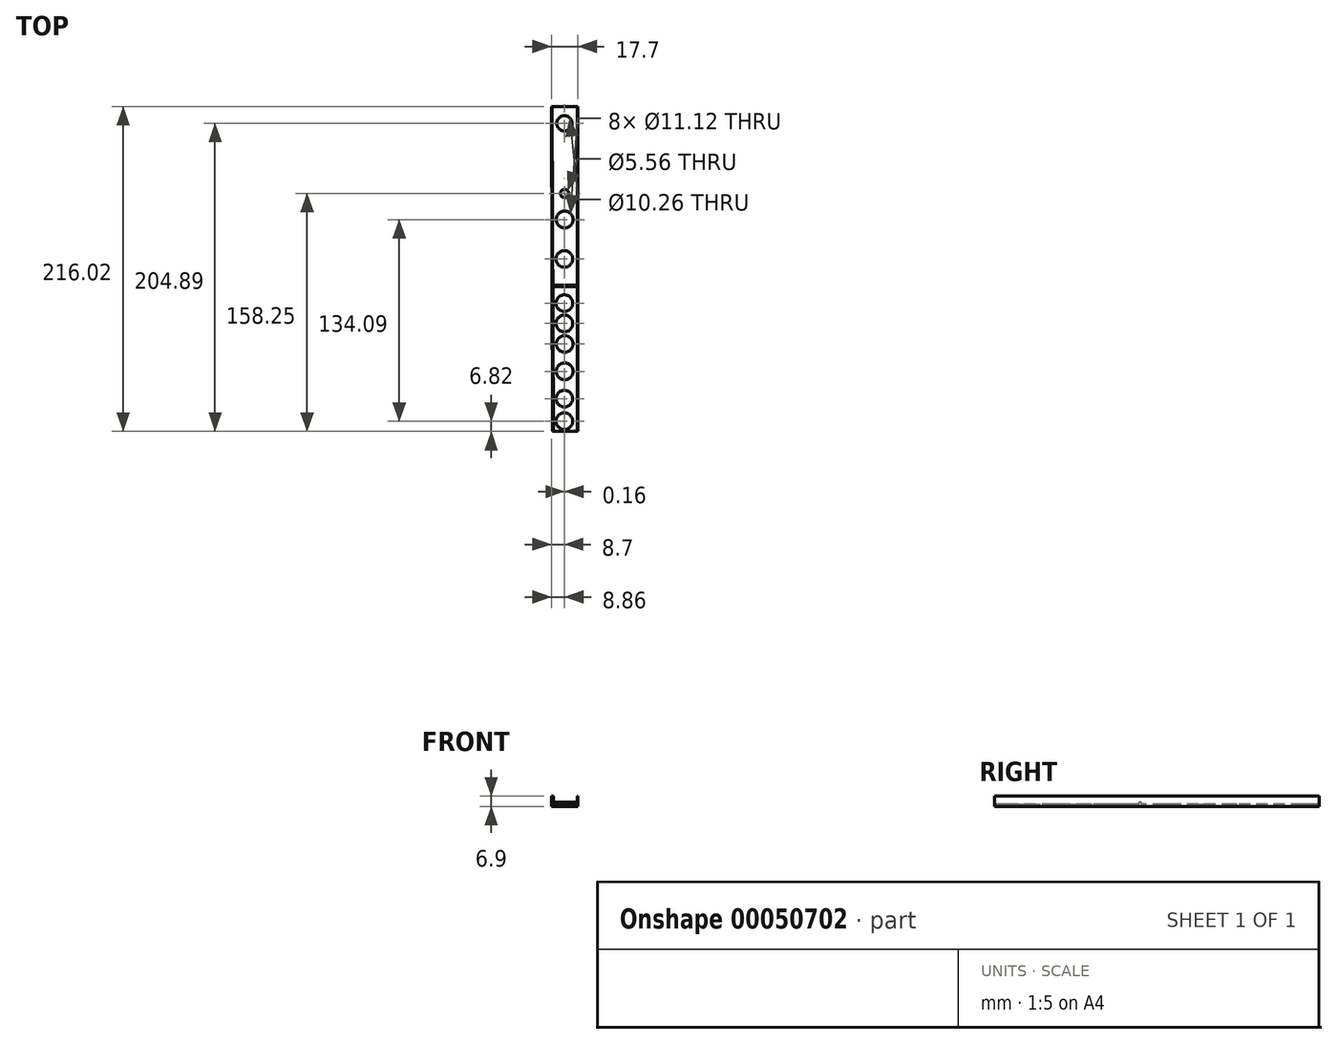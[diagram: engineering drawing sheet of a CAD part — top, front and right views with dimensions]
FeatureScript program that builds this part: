
annotation { "Feature Type Name" : "Feature", "Feature Type Description" : "" }
export const myFeature = defineFeature(function(context is Context, id is Id, definition is map)
    precondition{}
    {
        {
            var Q0;
            Q0=qCreatedBy(makeId("Top.planeOp"),FACE);
            var sketch = newSketch(context, id + "F0", { "sketchPlane" : qUnion([Q0])});
            skLineSegment(sketch, "E0", {"start": v(-8.7, 26.77) * mm, "end": v(9, 26.77) * mm});
            skLineSegment(sketch, "E1", {"start": v(9, 26.77) * mm, "end": v(9, -189.25) * mm});
            skLineSegment(sketch, "E2", {"start": v(9, -189.25) * mm, "end": v(-7.94, -189.25) * mm});
            skLineSegment(sketch, "E3", {"start": v(-7.94, -189.25) * mm, "end": v(-8.7, 26.77) * mm});
            skCircle(sketch, "E4", {"center": v(0, 15.64) * mm, "radius": 5.13 * mm});
            skCircle(sketch, "E5", {"center": v(0.16, -31) * mm, "radius": 2.78 * mm});
            skCircle(sketch, "E6", {"center": v(0.16, -48.34) * mm, "radius": 5.56 * mm});
            skCircle(sketch, "E7", {"center": v(0, -74.53) * mm, "radius": 5.56 * mm});
            skCircle(sketch, "E8", {"center": v(0, -103.97) * mm, "radius": 5.56 * mm});
            skCircle(sketch, "E9", {"center": v(0.15, -131.06) * mm, "radius": 5.56 * mm});
            skCircle(sketch, "E10", {"center": v(0, -117.43) * mm, "radius": 5.56 * mm});
            skCircle(sketch, "E11", {"center": v(0.15, -149.28) * mm, "radius": 5.56 * mm});
            skCircle(sketch, "E12", {"center": v(0, -167.44) * mm, "radius": 5.56 * mm});
            skCircle(sketch, "E13", {"center": v(0, -182.43) * mm, "radius": 5.56 * mm});
            skLineSegment(sketch, "E14", {"start": v(-8.7, 26.77) * mm, "end": v(-8.14, 26.77) * mm});
            skLineSegment(sketch, "E15", {"start": v(9, 26.77) * mm, "end": v(8.45, 26.77) * mm});
            skLineSegment(sketch, "E16", {"start": v(8.45, -189.25) * mm, "end": v(9, -189.25) * mm});
            skSolve(sketch);
        }
        {
            var Q0;
            Q0 = qSketchRegion(id + "F0", true);
            extrude(context, id + "F1", {"entities" : qUnion([Q0]), "depth" : 0.56 * mm});
        }
        {
            var Q0;
            Q0=makeQuery(id+"F1.opExtrude","SWEPT_FACE",FACE,{"disambiguationData":[OSD([sQuery(id+"F0.wireOp",EDGE,"E1")])]});
            var sketch = newSketch(context, id + "F2", { "sketchPlane" : qUnion([Q0])});
            skLineSegment(sketch, "E17", {"start": v(-189.25, 0.56) * mm, "end": v(-189.25, 6.9) * mm});
            skLineSegment(sketch, "E18", {"start": v(26.77, 6.9) * mm, "end": v(26.77, 0.56) * mm});
            skLineSegment(sketch, "E19", {"start": v(-189.25, 6.9) * mm, "end": v(26.77, 6.9) * mm});
            skSolve(sketch);
        }
        {
            var Q0;
            Q0=makeQuery(id+"F2.imprint","IMPRINT",FACE,{"disambiguationData":[TD([[makeQuery(id+"F2.imprint","IMPRINT",EDGE,{"derivedFrom":sQuery(id+"F2.wireOp",EDGE,"E17")}),-1.0]])]});
            extrude(context, id + "F3", {"entities" : qUnion([Q0]), "oppositeDirection" : true, "depth" : 0.56 * mm});
        }
        {
            var Q0;
            Q0=makeQuery(id+"F1.opExtrude","SWEPT_FACE",FACE,{"disambiguationData":[OSD([sQuery(id+"F0.wireOp",EDGE,"E3")])]});
            var sketch = newSketch(context, id + "F4", { "sketchPlane" : qUnion([Q0])});
            skLineSegment(sketch, "E20", {"start": v(-26.8, 0.56) * mm, "end": v(-26.8, 6.9) * mm});
            skLineSegment(sketch, "E21", {"start": v(189.22, 0.56) * mm, "end": v(189.22, 6.9) * mm});
            skLineSegment(sketch, "E22", {"start": v(189.22, 6.9) * mm, "end": v(-26.8, 6.9) * mm});
            skSolve(sketch);
        }
        {
            var Q0;
            Q0=makeQuery(id+"F4.imprint","IMPRINT",FACE,{"disambiguationData":[TD([[makeQuery(id+"F4.imprint","IMPRINT",EDGE,{"derivedFrom":sQuery(id+"F4.wireOp",EDGE,"E20")}),-1.0]])]});
            extrude(context, id + "F5", {"entities" : qUnion([Q0]), "oppositeDirection" : true, "depth" : 0.56 * mm});
        }
        {
            var Q0;
            Q0=makeQuery(id+"F1.opExtrude","CAP_FACE",FACE,{"disambiguationData":[OSD([sQuery(id+"F0.wireOp",EDGE,"E0"),sQuery(id+"F0.wireOp",EDGE,"E1"),sQuery(id+"F0.wireOp",EDGE,"E2"),sQuery(id+"F0.wireOp",EDGE,"E4"),sQuery(id+"F0.wireOp",EDGE,"E5"),sQuery(id+"F0.wireOp",EDGE,"E6"),sQuery(id+"F0.wireOp",EDGE,"E7"),sQuery(id+"F0.wireOp",EDGE,"E8"),sQuery(id+"F0.wireOp",EDGE,"E9"),sQuery(id+"F0.wireOp",EDGE,"E10"),sQuery(id+"F0.wireOp",EDGE,"E11"),sQuery(id+"F0.wireOp",EDGE,"E12"),sQuery(id+"F0.wireOp",EDGE,"E13"),sQuery(id+"F0.wireOp",EDGE,"E3"),sQuery(id+"F0.wireOp",EDGE,"E14"),sQuery(id+"F0.wireOp",EDGE,"E15"),sQuery(id+"F0.wireOp",EDGE,"E16")])],"isStart":false});
            var sketch = newSketch(context, id + "F6", { "sketchPlane" : qUnion([Q0])});
            skLineSegment(sketch, "E23", {"start": v(9, 26.77) * mm, "end": v(9, -91.85) * mm});
            skLineSegment(sketch, "E24", {"start": v(9, -91.85) * mm, "end": v(-8.28, -91.85) * mm});
            skLineSegment(sketch, "E25", {"start": v(-8.28, -91.85) * mm, "end": v(-8.28, -93.03) * mm});
            skLineSegment(sketch, "E26", {"start": v(-8.28, -93.03) * mm, "end": v(9, -92.97) * mm});
            skLineSegment(sketch, "E27", {"start": v(9, -92.97) * mm, "end": v(9, -91.85) * mm});
            skSolve(sketch);
        }
        {
            var Q0;
            Q0=makeQuery(id+"F6.imprint","IMPRINT",FACE,{"disambiguationData":[TD([[makeQuery(id+"F6.imprint","IMPRINT",EDGE,{"derivedFrom":sQuery(id+"F6.wireOp",EDGE,"E24")}),1.0]])]});
            var Q1;
            Q1=makeQuery(id+"F3.opExtrude","SWEPT_FACE",FACE,{"disambiguationData":[OSD([sQuery(id+"F2.wireOp",EDGE,"E19")])]});
            var Q2;
            Q2=makeQuery(id+"F5.opExtrude","SWEPT_FACE",FACE,{"disambiguationData":[OSD([sQuery(id+"F4.wireOp",EDGE,"E22")])]});
            extrude(context, id + "F7", {"entities" : qUnion([Q0, Q1, Q2]), "depth" : 1.12 * mm});
        }
        {
            var Q0;
            Q0=makeQuery(id+"F7.opExtrude","SWEPT_BODY",BODY,{"disambiguationData":[OSD([sQuery(id+"F2.wireOp",EDGE,"E19")])]});
            var Q1;
            Q1=makeQuery(id+"F7.opExtrude","SWEPT_BODY",BODY,{"disambiguationData":[OSD([sQuery(id+"F4.wireOp",EDGE,"E22")])]});
            deleteBodies(context, id + "F8", {"entities" : qUnion([Q0, Q1])});
        }
        {
            var Q0;
            Q0=makeQuery(id+"F3.opExtrude","SWEPT_BODY",BODY,{"disambiguationData":[OSD([sQuery(id+"F0.wireOp",EDGE,"E1"),sQuery(id+"F2.wireOp",EDGE,"E17"),sQuery(id+"F2.wireOp",EDGE,"E18"),sQuery(id+"F2.wireOp",EDGE,"E19")])]});
            var Q1;
            Q1=makeQuery(id+"F7.opExtrude","SWEPT_BODY",BODY,{"disambiguationData":[OSD([sQuery(id+"F6.wireOp",EDGE,"E24"),sQuery(id+"F6.wireOp",EDGE,"E25"),sQuery(id+"F6.wireOp",EDGE,"E26"),sQuery(id+"F6.wireOp",EDGE,"E27")])]});
            var Q2;
            Q2=makeQuery(id+"F1.opExtrude","SWEPT_BODY",BODY,{"disambiguationData":[OSD([sQuery(id+"F0.wireOp",EDGE,"E0"),sQuery(id+"F0.wireOp",EDGE,"E1"),sQuery(id+"F0.wireOp",EDGE,"E2"),sQuery(id+"F0.wireOp",EDGE,"E4"),sQuery(id+"F0.wireOp",EDGE,"E5"),sQuery(id+"F0.wireOp",EDGE,"E6"),sQuery(id+"F0.wireOp",EDGE,"E7"),sQuery(id+"F0.wireOp",EDGE,"E8"),sQuery(id+"F0.wireOp",EDGE,"E9"),sQuery(id+"F0.wireOp",EDGE,"E10"),sQuery(id+"F0.wireOp",EDGE,"E11"),sQuery(id+"F0.wireOp",EDGE,"E12"),sQuery(id+"F0.wireOp",EDGE,"E13"),sQuery(id+"F0.wireOp",EDGE,"E3"),sQuery(id+"F0.wireOp",EDGE,"E14"),sQuery(id+"F0.wireOp",EDGE,"E15"),sQuery(id+"F0.wireOp",EDGE,"E16")])]});
            var Q3;
            Q3=makeQuery(id+"F5.opExtrude","SWEPT_BODY",BODY,{"disambiguationData":[OSD([sQuery(id+"F0.wireOp",EDGE,"E3"),sQuery(id+"F4.wireOp",EDGE,"E20"),sQuery(id+"F4.wireOp",EDGE,"E21"),sQuery(id+"F4.wireOp",EDGE,"E22")])]});
            booleanBodies(context, id + "F9", {"operationType" : BooleanOperationType.UNION, "tools" : qUnion([Q0, Q1, Q2, Q3])});
        }
        {
            var Q0;
            {var subQ0=sQuery(id+"F0.wireOp",EDGE,"E6");var subQ2=sQuery(id+"F0.wireOp",EDGE,"E5");var subQ3=sQuery(id+"F0.wireOp",EDGE,"E4");var subQ4=sQuery(id+"F0.wireOp",EDGE,"E3");var subQ5=sQuery(id+"F0.wireOp",EDGE,"E15");var subQ6=sQuery(id+"F0.wireOp",EDGE,"E14");var subQ7=sQuery(id+"F0.wireOp",EDGE,"E0");var subQ8=sQuery(id+"F0.wireOp",EDGE,"E7");var subQ9=sQuery(id+"F0.wireOp",EDGE,"E1");Q0=makeQuery(id+"F9.opBoolean","SPLIT",FACE,{"disambiguationData":[TD([makeQuery(id+"F1.opExtrude","SWEPT_FACE",FACE,{"disambiguationData":[OSD([subQ3])]})])],"derivedFrom":makeQuery(id+"F1.opExtrude","CAP_FACE",FACE,{"disambiguationData":[OSD([subQ7,subQ9,sQuery(id+"F0.wireOp",EDGE,"E2"),subQ3,subQ2,subQ0,subQ8,sQuery(id+"F0.wireOp",EDGE,"E8"),sQuery(id+"F0.wireOp",EDGE,"E9"),sQuery(id+"F0.wireOp",EDGE,"E10"),sQuery(id+"F0.wireOp",EDGE,"E11"),sQuery(id+"F0.wireOp",EDGE,"E12"),sQuery(id+"F0.wireOp",EDGE,"E13"),subQ4,subQ6,subQ5,sQuery(id+"F0.wireOp",EDGE,"E16")])],"isStart":false})});}
            var Q1;
            {var subQ1=sQuery(id+"F0.wireOp",EDGE,"E1");var subQ2=sQuery(id+"F0.wireOp",EDGE,"E3");var subQ3=sQuery(id+"F0.wireOp",EDGE,"E13");var subQ4=sQuery(id+"F0.wireOp",EDGE,"E12");var subQ5=sQuery(id+"F0.wireOp",EDGE,"E11");var subQ6=sQuery(id+"F0.wireOp",EDGE,"E16");var subQ7=sQuery(id+"F0.wireOp",EDGE,"E2");var subQ8=sQuery(id+"F0.wireOp",EDGE,"E8");var subQ9=sQuery(id+"F0.wireOp",EDGE,"E9");var subQ10=sQuery(id+"F0.wireOp",EDGE,"E10");Q1=makeQuery(id+"F9.opBoolean","SPLIT",FACE,{"disambiguationData":[TD([makeQuery(id+"F1.opExtrude","SWEPT_FACE",FACE,{"disambiguationData":[OSD([subQ8])]})])],"derivedFrom":makeQuery(id+"F1.opExtrude","CAP_FACE",FACE,{"disambiguationData":[OSD([sQuery(id+"F0.wireOp",EDGE,"E0"),subQ1,subQ7,sQuery(id+"F0.wireOp",EDGE,"E4"),sQuery(id+"F0.wireOp",EDGE,"E5"),sQuery(id+"F0.wireOp",EDGE,"E6"),sQuery(id+"F0.wireOp",EDGE,"E7"),subQ8,subQ9,subQ10,subQ5,subQ4,subQ3,subQ2,sQuery(id+"F0.wireOp",EDGE,"E14"),sQuery(id+"F0.wireOp",EDGE,"E15"),subQ6])],"isStart":false})});}
            var Q2;
            Q2=makeQuery(id+"F7.opExtrude","CAP_FACE",FACE,{"disambiguationData":[OSD([sQuery(id+"F6.wireOp",EDGE,"E24"),sQuery(id+"F6.wireOp",EDGE,"E25"),sQuery(id+"F6.wireOp",EDGE,"E26"),sQuery(id+"F6.wireOp",EDGE,"E27")])],"isStart":false});
            extrude(context, id + "F10", {"entities" : qUnion([Q0, Q1, Q2]), "operationType" : NewBodyOperationType.ADD, "depth" : 1.12 * mm});
        }
    });
